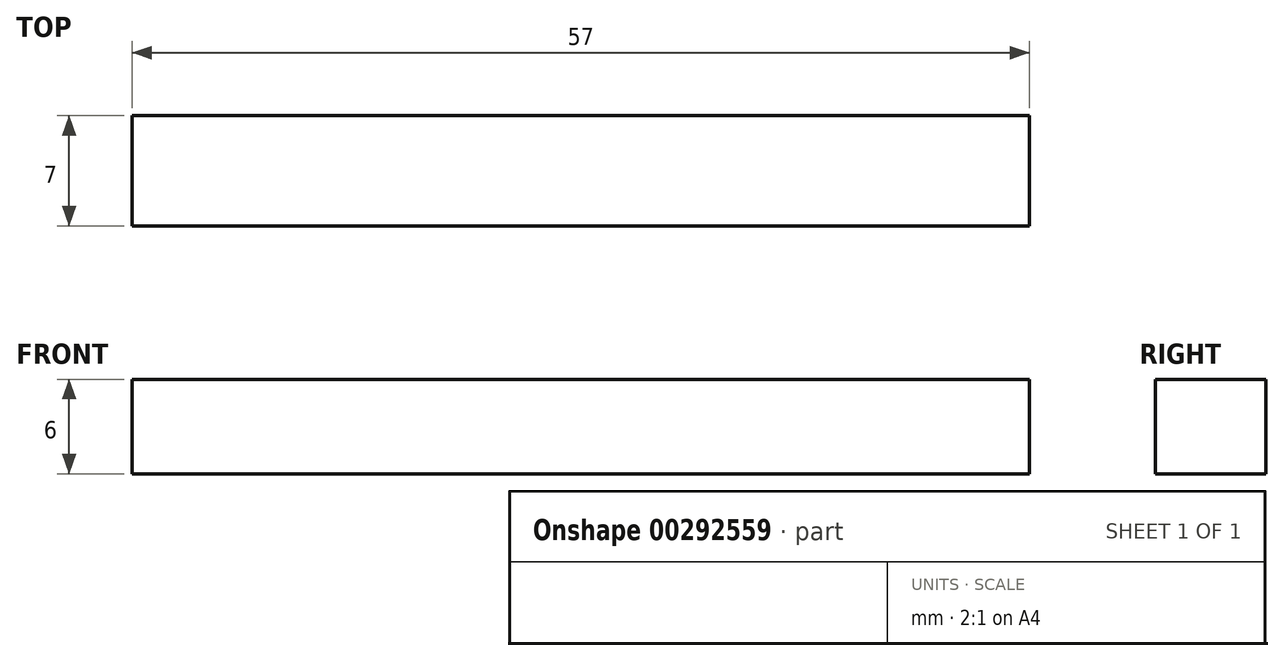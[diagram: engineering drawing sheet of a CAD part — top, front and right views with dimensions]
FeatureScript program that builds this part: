
annotation { "Feature Type Name" : "Feature", "Feature Type Description" : "" }
export const myFeature = defineFeature(function(context is Context, id is Id, definition is map)
    precondition{}
    {
        {
            var Q0;
            Q0=qCreatedBy(makeId("Front.planeOp"),FACE);
            var sketch = newSketch(context, id + "F0", { "sketchPlane" : qUnion([Q0])});
            skLineSegment(sketch, "E0", {"start": v(-29.34, -20.11) * mm, "end": v(27.66, -20.11) * mm});
            skLineSegment(sketch, "E1", {"start": v(27.66, -20.11) * mm, "end": v(27.66, -26.11) * mm});
            skLineSegment(sketch, "E2", {"start": v(-29.34, -20.11) * mm, "end": v(-29.34, -26.11) * mm});
            skLineSegment(sketch, "E3", {"start": v(-29.34, -26.11) * mm, "end": v(27.66, -26.11) * mm});
            skSolve(sketch);
        }
        {
            var Q0;
            Q0=sQuery(id+"F0.wireOp",EDGE,"E3");
            var Q1;
            Q1=sQuery(id+"F0.wireOp",EDGE,"E2");
            var Q2;
            Q2=sQuery(id+"F0.wireOp",EDGE,"E1");
            var Q3;
            Q3=sQuery(id+"F0.wireOp",EDGE,"E0");
            extrude(context, id + "F1", {"bodyType" : ToolBodyType.SURFACE, "surfaceEntities" : qUnion([Q0, Q1, Q2, Q3]), "depth" : 7 * mm});
        }
        {
            var Q0;
            Q0 = qSketchRegion(id + "F0", true);
            extrude(context, id + "F2", {"entities" : qUnion([Q0]), "depth" : 7 * mm});
        }
    });
